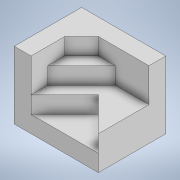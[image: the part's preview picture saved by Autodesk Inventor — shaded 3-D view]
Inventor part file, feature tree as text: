
AUTODESK INVENTOR PART (.ipt)
format: ipt  version: 2020 (Build 240168000, 168)  size: 135,680 bytes
history: native  units: mm
features: extrude x4, sketch x4, other x1, projected_geometry x1
ambient origin geometry x8: Origin, YZ Plane, XZ Plane, XY Plane, X Axis, Y Axis, Z Axis, Center Point
bodies: Body1 (feature_tree), Body2 (feature_tree)
feature tree (10):
  other  "實體1"
  extrude  "擠出1"  Depth=40.0mm
  extrude  "擠出2"  Depth=50.0mm
  extrude  "擠出3"  Depth=40.0mm TaperAngle=0.0deg
  extrude  "擠出4"  Depth=10.0mm
  sketch  "草圖1"
  sketch  "草圖2"
  projected_geometry  "投影迴路1"
  sketch  "草圖3"
  sketch  "草圖4"
